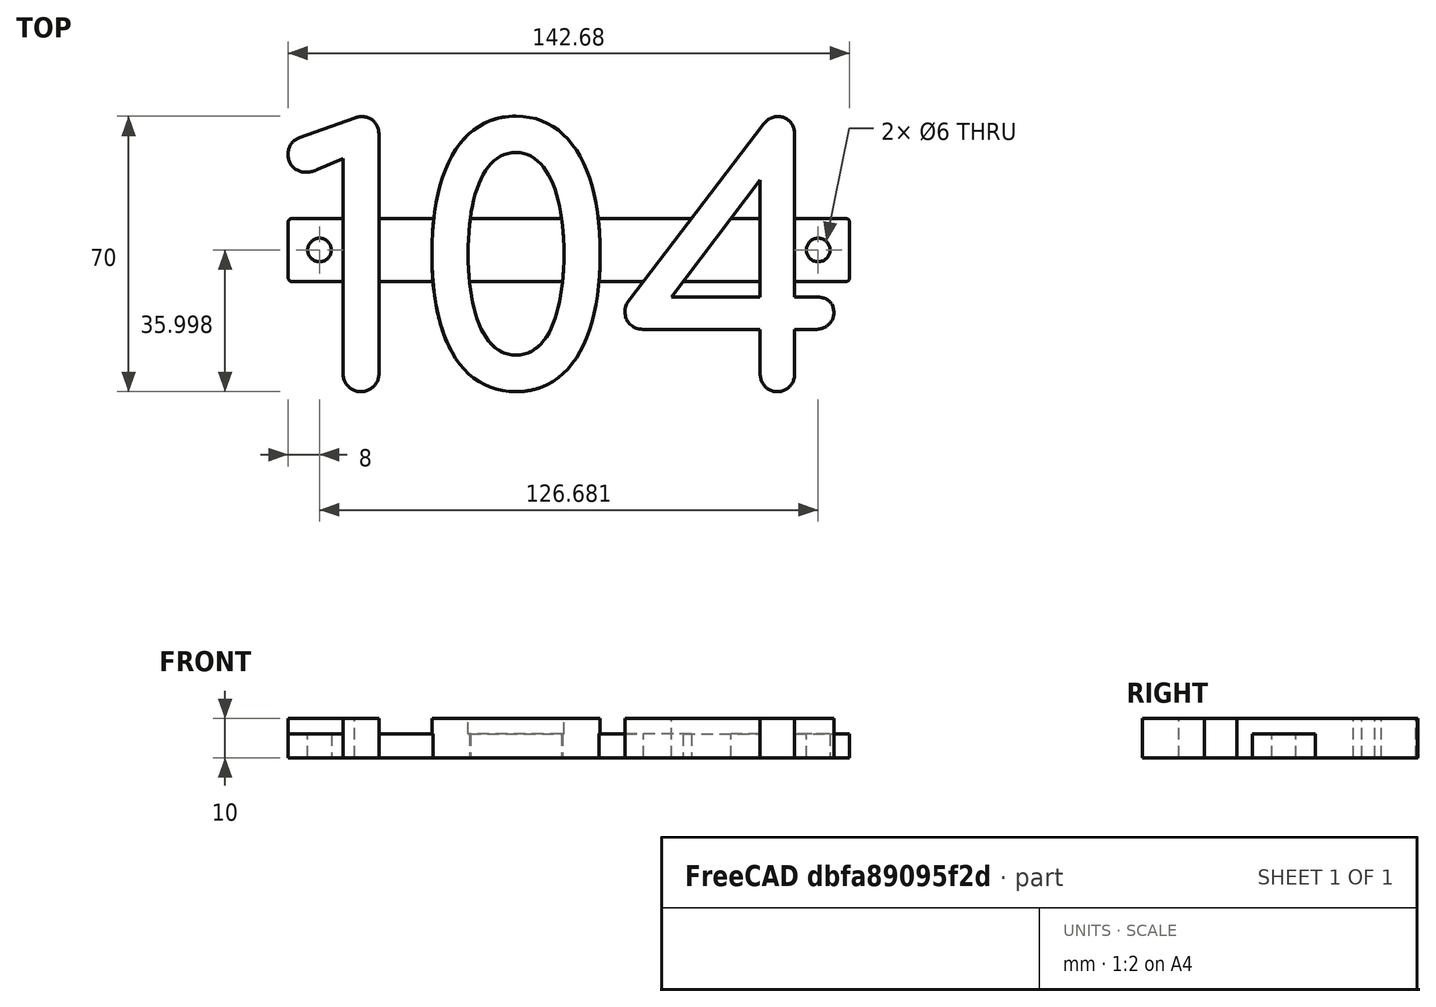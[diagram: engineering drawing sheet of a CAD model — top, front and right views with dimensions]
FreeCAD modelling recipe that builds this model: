
FCSTD DOCUMENT  (FreeCAD 1.2R20260401 (Git shallow))
Label: 104bellstpostbox
License: All rights reserved
LicenseURL: https://en.wikipedia.org/wiki/All_rights_reserved
objects: Sketcher::SketchObject×3, PartDesign::Pad×2, App::Point×1, PartDesign::Pocket×1, PartDesign::Fillet×1, PartDesign::Body×1
note: 19 computed .brp shape members not serialized (recipe doc carries the construction recipe); baked Part::Feature solids carry a one-line shape summary decoded from their .brp

FEATURE [App::Point] Origin001
  Role = Origin
FEATURE [Sketcher::SketchObject] Sketch
  ArcFitTolerance = 1e-06
  AttachmentSupport = -> [Origin]
  ExternalTypes = [0]
  FullyConstrained = false
  MakeInternals = false
  MapMode = 5
  _ExternalGeoVersion = 1
  sketch-geometry (38):
    g0: LineSegment [constr] StartX=0 StartY=126.188 StartZ=0 EndX=0 EndY=196.188 EndZ=0
    g1: BSplineCurve PolesCount=4 KnotsCount=2 Degree=3 IsPeriodic=0
    g2: LineSegment StartX=23.0946 StartY=130.753 StartZ=0 EndX=23.0946 EndY=191.443 EndZ=0
    g3: BSplineCurve PolesCount=4 KnotsCount=2 Degree=3 IsPeriodic=0
    g4: BSplineCurve PolesCount=4 KnotsCount=2 Degree=3 IsPeriodic=0
    g5: LineSegment StartX=16.9182 StartY=195.74 StartZ=0 EndX=2.95397 EndY=190.727 EndZ=0
    g6: BSplineCurve PolesCount=4 KnotsCount=2 Degree=3 IsPeriodic=0
    g7: BSplineCurve PolesCount=4 KnotsCount=2 Degree=3 IsPeriodic=0
    g8: BSplineCurve PolesCount=4 KnotsCount=2 Degree=3 IsPeriodic=0
    g9: LineSegment StartX=7.42967 StartY=182.581 StartZ=0 EndX=13.9642 EndY=185.356 EndZ=0
    g10: LineSegment StartX=13.9642 StartY=185.356 StartZ=0 EndX=13.9642 EndY=130.753 EndZ=0
    g11: BSplineCurve PolesCount=4 KnotsCount=2 Degree=3 IsPeriodic=0
    g12: BSplineCurve PolesCount=4 KnotsCount=2 Degree=3 IsPeriodic=0
    g13: BSplineCurve PolesCount=4 KnotsCount=2 Degree=3 IsPeriodic=0
    g14: BSplineCurve PolesCount=4 KnotsCount=2 Degree=3 IsPeriodic=0
    g15: BSplineCurve PolesCount=4 KnotsCount=2 Degree=3 IsPeriodic=0
    g16: BSplineCurve PolesCount=4 KnotsCount=2 Degree=3 IsPeriodic=0
    g17: BSplineCurve PolesCount=4 KnotsCount=2 Degree=3 IsPeriodic=0
    g18: BSplineCurve PolesCount=4 KnotsCount=2 Degree=3 IsPeriodic=0
    g19: BSplineCurve PolesCount=4 KnotsCount=2 Degree=3 IsPeriodic=0
    g20: BSplineCurve PolesCount=4 KnotsCount=2 Degree=3 IsPeriodic=0
    g21: LineSegment StartX=128.721 StartY=130.753 StartZ=0 EndX=128.721 EndY=142.032 EndZ=0
    g22: LineSegment StartX=128.721 StartY=142.032 StartZ=0 EndX=134.092 EndY=142.032 EndZ=0
    g23: BSplineCurve PolesCount=4 KnotsCount=2 Degree=3 IsPeriodic=0
    g24: BSplineCurve PolesCount=4 KnotsCount=2 Degree=3 IsPeriodic=0
    g25: LineSegment StartX=134.092 StartY=150.267 StartZ=0 EndX=128.721 EndY=150.267 EndZ=0
    g26: LineSegment StartX=128.721 StartY=150.267 StartZ=0 EndX=128.721 EndY=191.443 EndZ=0
    g27: BSplineCurve PolesCount=4 KnotsCount=2 Degree=3 IsPeriodic=0
    g28: BSplineCurve PolesCount=4 KnotsCount=2 Degree=3 IsPeriodic=0
    g29: LineSegment StartX=120.754 StartY=194.129 StartZ=0 EndX=86.4706 EndY=149.193 EndZ=0
    g30: BSplineCurve PolesCount=4 KnotsCount=2 Degree=3 IsPeriodic=0
    g31: LineSegment StartX=90.1407 StartY=142.032 StartZ=0 EndX=119.949 EndY=142.032 EndZ=0
    g32: LineSegment StartX=119.949 StartY=142.032 StartZ=0 EndX=119.949 EndY=130.753 EndZ=0
    g33: BSplineCurve PolesCount=4 KnotsCount=2 Degree=3 IsPeriodic=0
    g34: LineSegment StartX=119.949 StartY=150.267 StartZ=0 EndX=97.3913 EndY=150.267 EndZ=0
    g35: LineSegment StartX=97.3913 StartY=150.267 StartZ=0 EndX=119.949 EndY=179.896 EndZ=0
    g36: LineSegment StartX=119.949 StartY=179.896 StartZ=0 EndX=119.949 EndY=150.267 EndZ=0
    g37: LineSegment [constr] StartX=0 StartY=93.2903 StartZ=0 EndX=120 EndY=93.2903 EndZ=0
  constraints (7):
    c: Vertical(g0)
    c: DistanceY(g0,g0) = 70
    c: T21(g0,g1,g2)
    c: PointOnObject(g-1,g0)
    c: PointOnObject(g37,g-2)
    c: Horizontal(g37)
    c: DistanceX(g37,g37) = 120
FEATURE [PartDesign::Pad] Pad
  Direction = (0,0,1)
  Length = 10
  Length2 = 10
  Profile = -> Sketch
  ReferenceAxis = -> Sketch [N_Axis]
  Refine = true
  SideType = 0
  Suppressed = false
  Type = 0
  Type2 = 0
FEATURE [Sketcher::SketchObject] Sketch001
  ArcFitTolerance = 1e-06
  AttachmentSupport = -> [Origin]
  ExternalGeometry = -> [Pad]
  ExternalTypes = [0,0,0,0]
  FullyConstrained = true
  MakeInternals = false
  MapMode = 5
  _ExternalGeoVersion = 1
  sketch-geometry (4):
    g0: LineSegment StartX=0 StartY=170.188 StartZ=0 EndX=0 EndY=154.188 EndZ=0
    g1: LineSegment StartX=0 StartY=154.188 StartZ=0 EndX=142.681 EndY=154.188 EndZ=0
    g2: LineSegment StartX=142.681 StartY=154.188 StartZ=0 EndX=142.681 EndY=170.188 EndZ=0
    g3: LineSegment StartX=142.681 StartY=170.188 StartZ=0 EndX=0 EndY=170.188 EndZ=0
  constraints (12):
    c: Coincident(g0,g1)
    c: Coincident(g1,g2)
    c: Coincident(g2,g3)
    c: Coincident(g3,g0)
    c: Vertical(g0)
    c: Vertical(g2)
    c: Horizontal(g1)
    c: Horizontal(g3)
    c: PointOnObject(g0,g-2)
    c: DistanceX(g-5,g2) = 13.96
    c: DistanceY(g2,g2) = 16
    c: DistanceY(g-3,g0) = 28
FEATURE [PartDesign::Pad] Pad001
  BaseFeature = -> Pad
  Direction = (0,0,1)
  Length = 6
  Length2 = 10
  Profile = -> Sketch001
  ReferenceAxis = -> Sketch001 [N_Axis]
  Refine = true
  SideType = 0
  Suppressed = false
  Type = 0
  Type2 = 0
FEATURE [Sketcher::SketchObject] Sketch002
  ArcFitTolerance = 1e-06
  AttachmentSupport = -> [Pad001]
  ExternalGeometry = -> [Pad001]
  ExternalTypes = [0,0,0,0]
  FullyConstrained = true
  MakeInternals = false
  MapMode = 5
  Placement = pos=(0,0,6) rot=(0,0,1;0rad)
  _ExternalGeoVersion = 1
  sketch-geometry (2):
    g0: Circle CenterX=8 CenterY=162.188 CenterZ=0 NormalX=0 NormalY=0 NormalZ=1 AngleXU=0 Radius=3
    g1: Circle CenterX=134.681 CenterY=162.188 CenterZ=0 NormalX=0 NormalY=0 NormalZ=1 AngleXU=0 Radius=3
  constraints (6):
    c: Equal(g0,g1)
    c: Diameter(g1) = 6
    c: DistanceY(g1,g-3) = 8
    c: DistanceX(g1,g-3) = 8
    c: Horizontal(g0,g1)
    c: DistanceX(g-4,g0) = 8
FEATURE [PartDesign::Pocket] Pocket
  BaseFeature = -> Pad001
  Direction = (0,0,-1)
  Length = 5
  Length2 = 5
  Profile = -> Sketch002
  ReferenceAxis = -> Sketch002 [N_Axis]
  Refine = true
  SideType = 0
  Suppressed = false
  Type = 1
  Type2 = 0
FEATURE [PartDesign::Fillet] Fillet
  Base = -> Pocket [Edge114,Edge107,Edge129,Edge128]
  BaseFeature = -> Pocket
  Radius = 1
  Refine = true
  SupportTransform = false
  Suppressed = false
  UseAllEdges = false
FEATURE [PartDesign::Body] Body
  AllowCompound = true
  Group = -> [Sketch,Pad,Sketch001,Pad001,Sketch002,Pocket,Fillet]
  Origin = -> Origin
  Tip = -> Fillet
